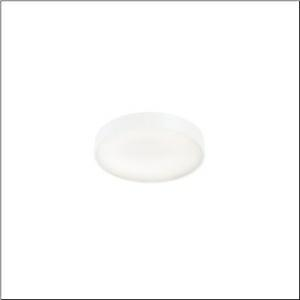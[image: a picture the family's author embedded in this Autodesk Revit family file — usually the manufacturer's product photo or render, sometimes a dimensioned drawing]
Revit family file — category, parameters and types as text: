
# Revit family: round_21_s_51mr34nd0421w
name_source: partatom
category: Lighting Fixtures
units: mm (PartAtom-declared; Revit-internal decimal feet)

## family parameters
Cut with Voids When Loaded = No
Host = Face
Light Source = No
Part Type = Normal
Room Calculation Point = No
Round Connector Dimension = Use Diameter
Shared = No

## types (1)
- Round 21 S (1 x LED, 3810 lm, 28.3 W, 4000K)
    Apparent Load = 28 VA
    CIE Flux Codes = 66 90 98 71 100
    Color Rendering = 80
    Color Temperature = 4000K
    Default Elevation = 1800 mm
    Description = Round 21 S, wall and ceiling luminaire, primary optical cover: micro prismatic cover, of PMMA, transparent, CAT 2 (L<= 3000cd/m²), light emission: direct/indirect distribution, primary light characteristic: symmetric, installation type: surface-mounted, suspended mounting, LED, rated luminous flux: 3.800lm, luminous efficacy: 135lm/W, light colour: 840, colour temperature: 4000K, control gear: DALI 2, with terminal, 5-pole, mains connection: 230V, AC, 50/60Hz, rated input power: 28.3W, housing, of aluminium, coated, white, diameter: 400mm, height: 62mm, protection rating (complete): IP40, insulation class (complete): insulation class I (protective earthing), certification: CE, impact resistance: IK04, permissible operating ambient temperature: -10..+35°C, packaging unit: 1 piece
    Height = 87 mm
    Lamp = 1 x LED
    Lamp Light Flux = 3810 lm
    Lamp Power = 28.3 W
    Lamp count = 1
    Length = 400 mm
    Luminous efficacy = 135 lm/W
    Manufacturer = Siteco
    ModVariant = No
    Model = 51MR34ND0421W
    Mounting Place = Ceiling
    Mounting Type = Surface mounted
    Number of Poles = 1
    OnlyDefault = Yes
    Power Factor = 1
    Product Name = Round 21 S
    Product group = wall and ceiling luminaire
    ProductGroupID = 304
    Protection Class = Protection class I
    Protection Degree = IP 40
    RLX_Detail_Level = 1
    RLX_Emergency_Light_Flux = 0 lm
    RLX_Emergency_Type = 0
    RLX_Emergency_Type_DB = No
    RlxData = <blob elided: 12845 chars, md5=1a093c20>
    Socket = socket
    Standby Power = 0 W
    System Light Flux = 3810 lm
    System Power = 28 W
    Type Comments = Product without accessories
    Type Image = l_1258334.jpg
    URL = http://relux.com
    VarID = ---
    Voltage = 0 V
    Weight = 0.00 kg
    Width = 0 mm  [stored 0 ft]

note: [stored X ft] marks values corroborated as IEEE doubles in the binary element streams (Revit-internal decimal feet)

## geometry (parser evidence)
native form markers: Sweep x12
no freeform markers — native parametric forms only
